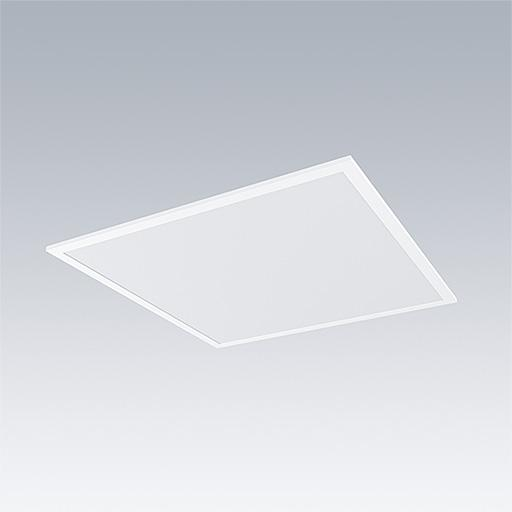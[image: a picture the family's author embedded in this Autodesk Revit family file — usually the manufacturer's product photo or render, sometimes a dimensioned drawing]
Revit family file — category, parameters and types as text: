
# Revit family: Thorn BETA FORCE
name_source: partatom
category: Lighting Fixtures
units: mm (PartAtom-declared; Revit-internal decimal feet)

## family parameters
Cut with Voids When Loaded = Yes
Host = Face
Light Source = Yes
Maintain Annotation Orientation = No
OmniClass Number = 23.80.70.11.11
OmniClass Title = General Luminaries, Non Directional
Part Type = Normal
Room Calculation Point = Yes
Round Connector Dimension = Use Diameter
Shared = No

## types (17) — shared parameters
Assembly Code = Pr_70_60_48_45
Color Filter = 16777215
Description = Recessed Modular Luminaire
Dimming Lamp Color Temperature Shift = <None>
Emit Shape Visible in Rendering = Yes
Housing Q625 = No
Luminaire Height = 35 mm  [stored 0.114829 ft]
Manufacturer = Thorn Lighting
Plasterboard Kit = No
Power Factor = 0.9
SELECT HOUSING TYPE = SELECT HOUSING TYPE
SELECT MOUNTING ACCESSORIES = SELECT MOUNTING ACCESSORIES
Tilt Angle = -90.00°
Type Plasterboard kit 3X12 = Thorn BETA 3 Plasterboard Kit : BETA 3 PLASTERBOARD KIT 3x12
Type Plasterboard kit Q600 = Thorn BETA 3 Plasterboard Kit : BETA 3 PLASTERBOARD KIT Q600
Type Plasterboard kit Q625 = Thorn BETA 3 Plasterboard Kit : BETA 3 PLASTERBOARD KIT Q625
URL = https://www.thornlighting.com
Visibility Plasterboard kit = No
Voltage = 230 V
zero-valued in all types: Default Elevation, Void

## per-type parameters (varying)
| type | Apparent Load | Emit from Rectangle Length | Emit from Rectangle Width | Frame | Housing 3X12 | Housing 3X12D | Housing Q600 | Luminaire Length | Luminaire Width | Model | Photometric Web File | Type Image | Type Plasterboard Kit |
| BETA FORCE 3500-80 CSW OP HFIX 3X12 | 25 VA | 1160 mm  [stored 3.80577 ft] | 260 mm  [stored 0.853018 ft] | 19 mm  [stored 0.062336 ft] | Yes | No | No | 1196 mm  [stored 3.92388 ft] | 296 mm  [stored 0.971129 ft] | 96638055 | 96638055_(4000K).IES | Beta Force-3x12.jpg | Thorn BETA 3 Plasterboard Kit : BETA 3 PLASTERBOARD KIT 3x12 |
| BETA FORCE 4100-80 CSW OP HFIX 3X12 | 31 VA | 1160 mm  [stored 3.80577 ft] | 260 mm  [stored 0.853018 ft] | 19 mm  [stored 0.062336 ft] | Yes | No | No | 1196 mm  [stored 3.92388 ft] | 296 mm  [stored 0.971129 ft] | 96638056 | 96638056_(4000K).IES | Beta Force-3x12.jpg | Thorn BETA 3 Plasterboard Kit : BETA 3 PLASTERBOARD KIT 3x12 |
| BETA FORCE 3500-80 CSW OP HFIX Q600 | 25 VA | 560 mm  [stored 1.83727 ft] | 560 mm  [stored 1.83727 ft] | 16.5 mm  [stored 0.0541339 ft] | No | No | Yes | 596 mm  [stored 1.95538 ft] | 596 mm  [stored 1.95538 ft] | 96638052 | 96638052_(4000K).IES | Beta Force-600.jpg | Thorn BETA 3 Plasterboard Kit : BETA 3 PLASTERBOARD KIT Q600 |
| BETA FORCE 4100-80 CSW OP HFIX Q600 | 30 VA | 560 mm  [stored 1.83727 ft] | 560 mm  [stored 1.83727 ft] | 16.5 mm  [stored 0.0541339 ft] | No | No | Yes | 596 mm  [stored 1.95538 ft] | 596 mm  [stored 1.95538 ft] | 96638053 | 96638053_(4000K).IES | Beta Force-600.jpg | Thorn BETA 3 Plasterboard Kit : BETA 3 PLASTERBOARD KIT Q600 |
| BETA FORCE 4100-90 CSW OP HFIX Q600 | 33 VA | 560 mm  [stored 1.83727 ft] | 560 mm  [stored 1.83727 ft] | 16.5 mm  [stored 0.0541339 ft] | No | No | Yes | 596 mm  [stored 1.95538 ft] | 596 mm  [stored 1.95538 ft] | 96638058 | 96638058_(4000K).IES | Beta Force-600.jpg | Thorn BETA 3 Plasterboard Kit : BETA 3 PLASTERBOARD KIT Q600 |
| BETA FORCE 6000-80 CSW OP HFIX Q600 | 48 VA | 560 mm  [stored 1.83727 ft] | 560 mm  [stored 1.83727 ft] | 16.5 mm  [stored 0.0541339 ft] | No | No | Yes | 596 mm  [stored 1.95538 ft] | 596 mm  [stored 1.95538 ft] | 96638054 | 96638054_(4000K).IES | Beta Force-600.jpg | Thorn BETA 3 Plasterboard Kit : BETA 3 PLASTERBOARD KIT Q600 |
| BETA FORCE 4100-90 CSW OP HFIX 3X12 | 33 VA | 1160 mm  [stored 3.80577 ft] | 260 mm  [stored 0.853018 ft] | 19 mm  [stored 0.062336 ft] | Yes | No | No | 1196 mm  [stored 3.92388 ft] | 296 mm  [stored 0.971129 ft] | 96638059 | 96638059_(4000K).IES | Beta Force-3x12.jpg | Thorn BETA 3 Plasterboard Kit : BETA 3 PLASTERBOARD KIT 3x12 |
| BETA FORCE 6000-80 CSW OP HFIX 3X12 | 49 VA | 1160 mm  [stored 3.80577 ft] | 260 mm  [stored 0.853018 ft] | 19 mm  [stored 0.062336 ft] | Yes | No | No | 1196 mm  [stored 3.92388 ft] | 296 mm  [stored 0.971129 ft] | 96638057 | 96638057_(4000K).IES | Beta Force-3x12.jpg | Thorn BETA 3 Plasterboard Kit : BETA 3 PLASTERBOARD KIT 3x12 |
| BETA FORCE 3500-80 CSW OP HF 3X12 | 26 VA | 1160 mm  [stored 3.80577 ft] | 260 mm  [stored 0.853018 ft] | 19 mm  [stored 0.062336 ft] | Yes | No | No | 1196 mm  [stored 3.92388 ft] | 296 mm  [stored 0.971129 ft] | 96638044 | 96638044_(4000K).IES | Beta Force-3x12.jpg | Thorn BETA 3 Plasterboard Kit : BETA 3 PLASTERBOARD KIT 3x12 |
| BETA FORCE 3500-80 CSW OP HF Q600 | 26 VA | 560 mm  [stored 1.83727 ft] | 560 mm  [stored 1.83727 ft] | 16.5 mm  [stored 0.0541339 ft] | No | No | Yes | 596 mm  [stored 1.95538 ft] | 596 mm  [stored 1.95538 ft] | 96638041 | 96638041_(4000K).IES | Beta Force-600.jpg | Thorn BETA 3 Plasterboard Kit : BETA 3 PLASTERBOARD KIT Q600 |
| BETA FORCE 4100-80 CSW OP HF 3X12 | 31 VA | 1160 mm  [stored 3.80577 ft] | 260 mm  [stored 0.853018 ft] | 19 mm  [stored 0.062336 ft] | Yes | No | No | 1196 mm  [stored 3.92388 ft] | 296 mm  [stored 0.971129 ft] | 96638045 | 96638045_(4000K).IES | Beta Force-3x12.jpg | Thorn BETA 3 Plasterboard Kit : BETA 3 PLASTERBOARD KIT 3x12 |
| BETA FORCE 4100-80 CSW OP HF Q600 | 30 VA | 560 mm  [stored 1.83727 ft] | 560 mm  [stored 1.83727 ft] | 16.5 mm  [stored 0.0541339 ft] | No | No | Yes | 596 mm  [stored 1.95538 ft] | 596 mm  [stored 1.95538 ft] | 96638042 | 96638042_(4000K).IES | Beta Force-600.jpg | Thorn BETA 3 Plasterboard Kit : BETA 3 PLASTERBOARD KIT Q600 |
| BETA FORCE 4100-90 CSW OP HF 3X12 | 33 VA | 1160 mm  [stored 3.80577 ft] | 260 mm  [stored 0.853018 ft] | 19 mm  [stored 0.062336 ft] | Yes | No | No | 1196 mm  [stored 3.92388 ft] | 296 mm  [stored 0.971129 ft] | 96638051 | 96638051_(4000K).IES | Beta Force-3x12.jpg | Thorn BETA 3 Plasterboard Kit : BETA 3 PLASTERBOARD KIT 3x12 |
| BETA FORCE 4100-90 CSW OP HF Q600 | 34 VA | 560 mm  [stored 1.83727 ft] | 560 mm  [stored 1.83727 ft] | 16.5 mm  [stored 0.0541339 ft] | No | No | Yes | 596 mm  [stored 1.95538 ft] | 596 mm  [stored 1.95538 ft] | 96638050 | 96638050_(4000K).IES | Beta Force-600.jpg | Thorn BETA 3 Plasterboard Kit : BETA 3 PLASTERBOARD KIT Q600 |
| BETA FORCE 6000-80 CSW OP HF 3X12 | 47 VA | 1160 mm  [stored 3.80577 ft] | 260 mm  [stored 0.853018 ft] | 19 mm  [stored 0.062336 ft] | Yes | No | No | 1196 mm  [stored 3.92388 ft] | 296 mm  [stored 0.971129 ft] | 96638046 | 96638046_(4000K).IES | Beta Force-3x12.jpg | Thorn BETA 3 Plasterboard Kit : BETA 3 PLASTERBOARD KIT 3x12 |
| BETA FORCE 6000-80 CSW OP HF 3X12D | 47 VA | 1211 mm | 273 mm | 19 mm  [stored 0.062336 ft] | No | Yes | No | 1247 mm  [stored 4.09121 ft] | 309 mm  [stored 1.01378 ft] | 96638049 | 96638049_(4000K).IES | Beta Force-3x12.jpg | Thorn BETA 3 Plasterboard Kit : BETA 3 PLASTERBOARD KIT Q600 |
| BETA FORCE 6000-80 CSW OP HF Q600 | 46 VA | 560 mm  [stored 1.83727 ft] | 560 mm  [stored 1.83727 ft] | 16.5 mm  [stored 0.0541339 ft] | No | No | Yes | 596 mm  [stored 1.95538 ft] | 596 mm  [stored 1.95538 ft] | 96638043 | 96638043_(4000K).IES | Beta Force-600.jpg | Thorn BETA 3 Plasterboard Kit : BETA 3 PLASTERBOARD KIT Q600 |

note: [stored X ft] marks values corroborated as IEEE doubles in the binary element streams (Revit-internal decimal feet)

## geometry (parser evidence)
native form markers: Sweep x6
no freeform markers — native parametric forms only
